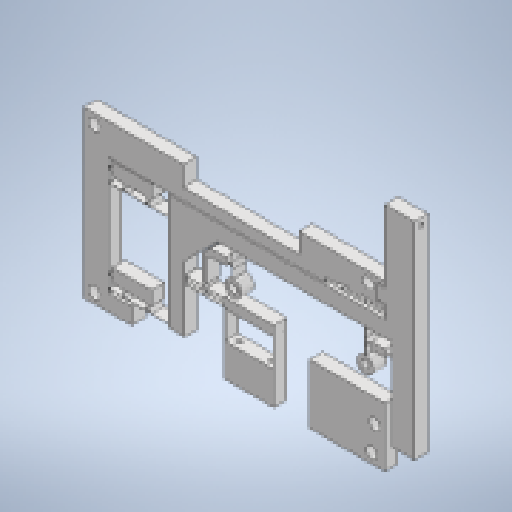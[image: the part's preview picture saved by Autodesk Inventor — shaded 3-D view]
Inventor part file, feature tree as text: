
AUTODESK INVENTOR PART (.ipt)
format: ipt  version: 2023 (Build 270158000, 158)  size: 600,576 bytes
history: native  units: mm
features: reference x11, extrude x10, sketch x9, other x6
ambient origin geometry x8: Origin, YZ Plane, XZ Plane, XY Plane, X Axis, Y Axis, Z Axis, Center Point
bodies: Solid1 (feature_tree)
feature tree (36):
  extrude  "Extrusion1"  Depth=20.0mm
  extrude  "Extrusion2"  Depth=4.0mm TaperAngle=0.0deg
  extrude  "Extrusion3"  Depth=0.5mm
  extrude  "Extrusion4"  Depth=5.0mm
  extrude  "Extrusion5"  Depth=18.0mm
  extrude  "Extrusion7"  Depth=1.0mm
  extrude  "Extrusion8"  Depth=1.0mm
  extrude  "Extrusion9"  Depth=0.1mm
  extrude  "Extrusion10"  Depth=5.0mm
  extrude  "Extrusion11"  Depth=0.1mm
  sketch  "Sketch1"  dims[d0=4.0mm d1=0.0mm d2=20.0mm]
  reference  "Reference1"
  sketch  "Sketch2"  dims[d3=9.0mm d4=4.0mm d5=0.0mm]
  sketch  "Sketch6"  dims[d6=7.0mm d7=0.5mm]
  reference  "Reference2"
  sketch  "Sketch7"  dims[d8=4.0mm d9=0.0mm d27=5.0mm]
  sketch  "Sketch9"  dims[d28=30.0mm d29=18.0mm]
  sketch  "Sketch10"  dims[d30=0.1mm d31=1.0mm]
  sketch  "Sketch11"  dims[d32=0.1mm d33=1.0mm]
  reference  "Reference3"
  reference  "Reference4"
  reference  "Reference5"
  reference  "Reference6"
  reference  "Reference7"
  reference  "Reference8"
  sketch  "Sketch12"  dims[d34=15.0mm d35=0.1mm]
  reference  "Reference9"
  reference  "Reference10"
  reference  "Reference11"
  sketch  "Sketch13"  dims[d37=5.0mm d39=5.0mm d40=0.1mm d41=0.1mm d43=0.0mm d44=15.0mm d45=18.0mm d46=2.0mm d47=0.1mm d48=40.0mm d49=2.4mm d50=2.4mm d51=5.0mm d52=5.0mm d53=0.1mm d54=0.05mm d55=0.05mm d56=0.1mm d57=8.0mm d58=0.1mm d59=2.0mm d60=1.5mm d61=5.0mm d62=0.5mm d63=0.5mm d64=0.1mm d65=0.1mm d66=5.0mm d67=0.0mm d68=0.0mm d69=15.0mm d70=10.0mm d71=15.0mm d72=0.0mm d73=1.5mm d74=1.5mm d75=0.2mm d76=0.2mm d79=1.0mm d80=0.1mm d81=0.1mm d82=1.0mm d83=4.0mm d84=0.0mm d87=15.0mm d88=10.0mm d89=10.0mm d90=10.0mm d91=10.0mm d92=0.1mm d93=0.75mm d94=2.0mm d95=1.5mm d97=18.0mm d98=7.0mm d99=4.0mm d100=0.0mm d105=2.0mm d106=6.9mm d107=20.0mm d108=35.0mm d110=6.0mm d111=4.0mm d112=0.0mm d113=2.0mm d114=2.0mm d115=10.0mm d116=2.5mm d117=1.6mm d118=1.6mm d119=10.0mm d120=0.0mm d121=30.0mm d122=10.0mm d123=0.0mm d124=13.0mm d125=3.0mm d126=3.0mm d127=4.0mm d128=3.4mm d129=3.4mm d130=0.1mm d131=7.0mm d132=5.0mm d133=8.0mm d134=0.0mm d135=12.0mm d140=-1.0mm d141=1.0mm d142=2.0mm d143=2.0mm d144=2.1mm d145=2.0mm d146=2.0mm d147=2.1mm d148=0.0mm d149=1.0mm d150=1.0mm d151=2.0mm d152=2.0mm d153=5.0mm d154=1.6mm d155=5.0mm d156=1.6mm d157=1.0mm d158=1.0mm d159=1.0mm d160=1.0mm d161=1.1mm d162=1.1mm d163=5.45mm d164=5.45mm d165=1.0mm d166=1.0mm d167=5.0mm d168=2.0mm d169=2.1mm d170=2.0mm d171=5.0mm d172=2.1mm d173=2.0mm d174=2.0mm d176=2.0mm d177=2.0mm d178=2.1mm d179=2.0mm d180=2.0mm d181=5.0mm d182=2.1mm d183=5.0mm d184=2.1mm d185=2.0mm d186=2.0mm d187=2.0mm d188=2.0mm d189=2.1mm d190=2.1mm d191=2.9mm d192=2.9mm d193=1.1mm d194=0.0mm d195=2.0mm d196=2.0mm d197=0.51mm d198=20.0mm d199=0.0mm d24=0.5mm d25=0.872665mm d26=0.5mm]
  other  "<userpath>\ClawdDrive\Objet3D\IminaProbe\V3Roue\RoueV3.iam"
  other  "RoueV3.iam"
  other  "RoueV3partA:1"
  other  "DifferentialLinearActuator:1"
  other  "RoueV3PartC:1"
  other  "DifferentialLinearActuator:5"
